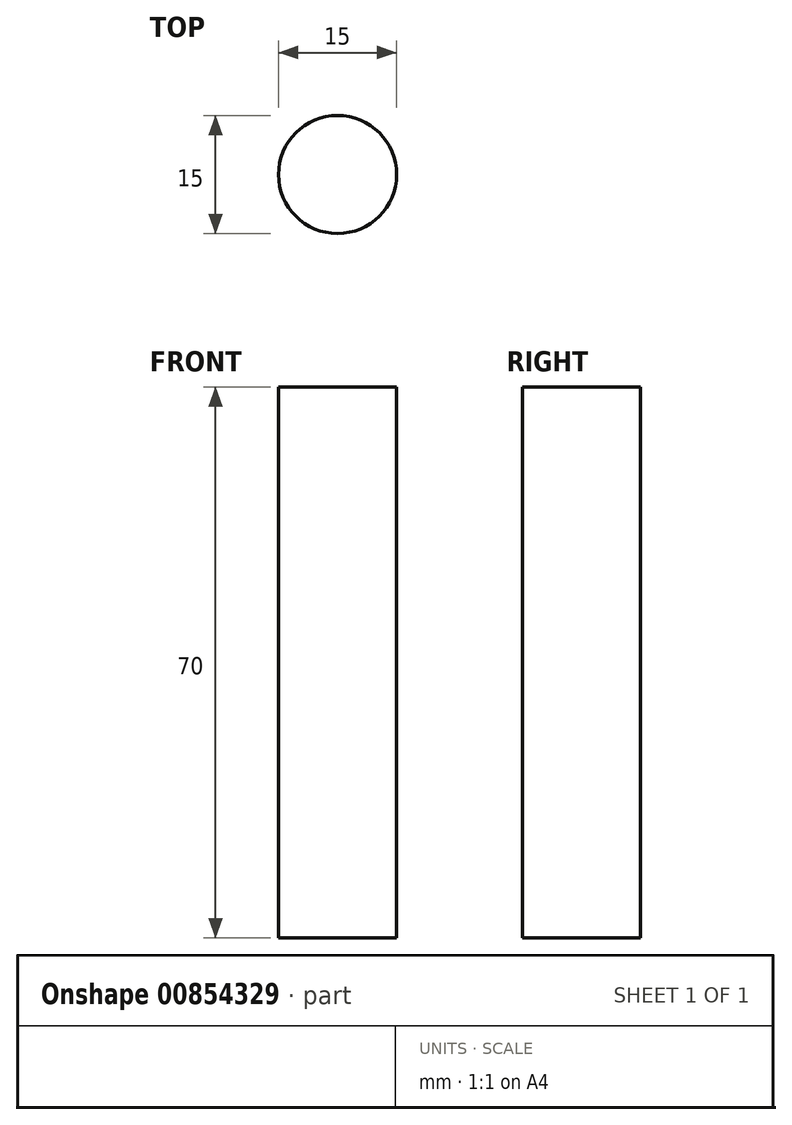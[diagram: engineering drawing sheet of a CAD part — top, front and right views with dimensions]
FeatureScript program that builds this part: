
annotation { "Feature Type Name" : "Feature", "Feature Type Description" : "" }
export const myFeature = defineFeature(function(context is Context, id is Id, definition is map)
    precondition{}
    {
        {
            var Q0;
            Q0=qCreatedBy(makeId("Top.planeOp"),FACE);
            var sketch = newSketch(context, id + "F0", { "sketchPlane" : qUnion([Q0])});
            skCircle(sketch, "E0", {"center": v(0, 0) * mm, "radius": 7.5 * mm});
            skSolve(sketch);
        }
        {
            var Q0;
            Q0=makeQuery(id+"F0.imprint","IMPRINT",FACE,{"disambiguationData":[TD([[makeQuery(id+"F0.imprint","IMPRINT",EDGE,{"derivedFrom":sQuery(id+"F0.wireOp",EDGE,"E0")}),1.0]])]});
            extrude(context, id + "F1", {"entities" : qUnion([Q0]), "depth" : 70 * mm, "offsetDistance" : 25 * mm});
        }
    });
